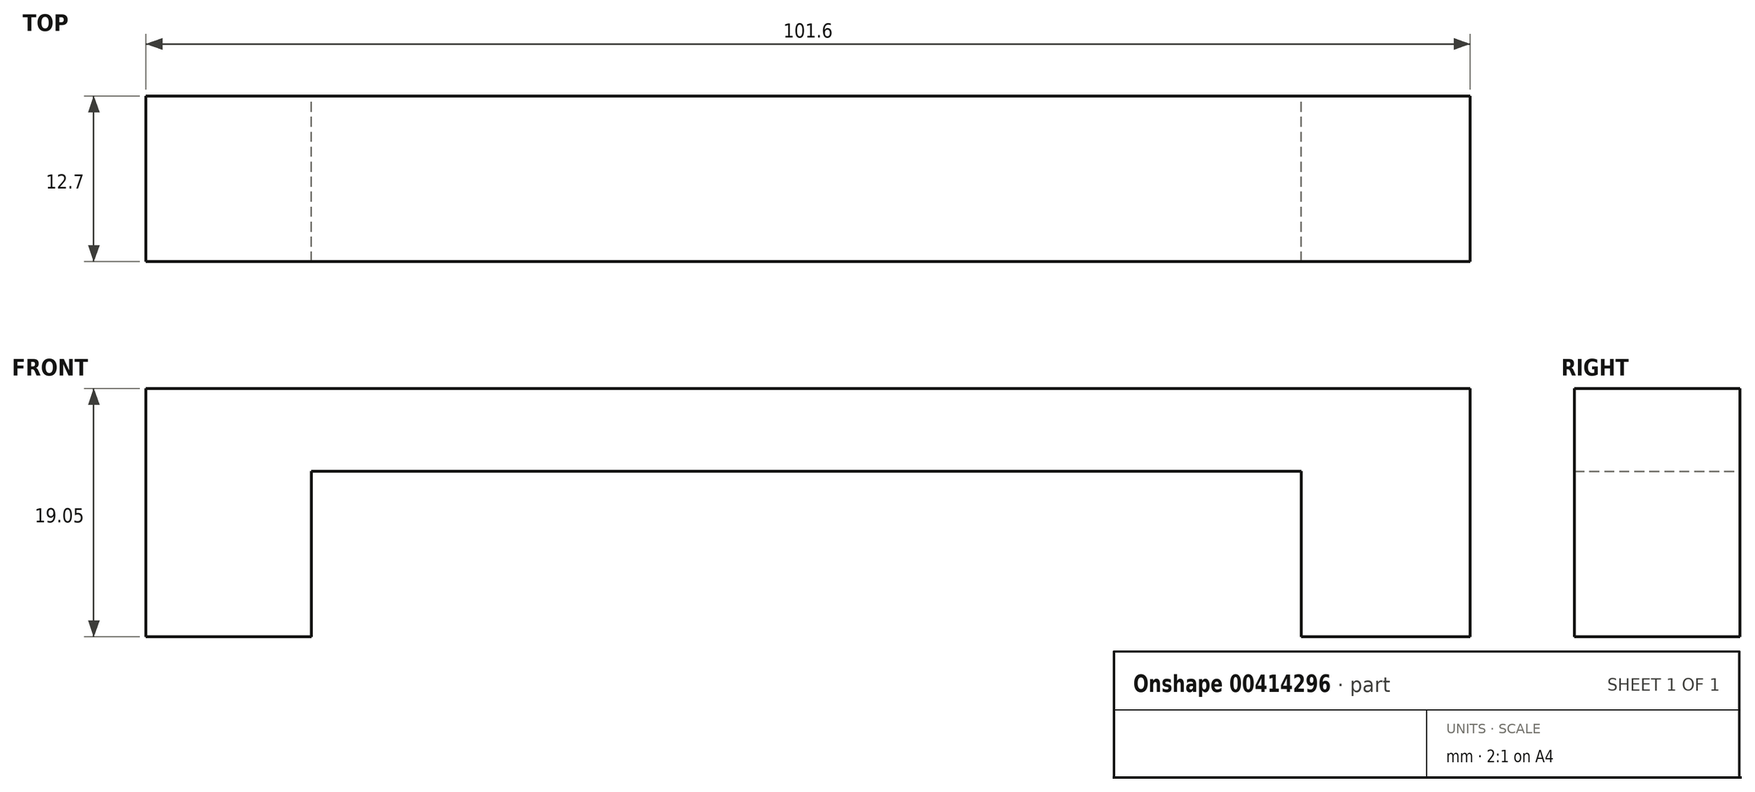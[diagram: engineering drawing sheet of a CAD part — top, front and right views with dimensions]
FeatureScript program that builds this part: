
annotation { "Feature Type Name" : "Feature", "Feature Type Description" : "" }
export const myFeature = defineFeature(function(context is Context, id is Id, definition is map)
    precondition{}
    {
        {
            var Q0;
            Q0=qCreatedBy(makeId("Front.planeOp"),FACE);
            var sketch = newSketch(context, id + "F0", { "sketchPlane" : qUnion([Q0])});
            skLineSegment(sketch, "E0", {"start": v(0, 0) * mm, "end": v(0, 19.05) * mm});
            skLineSegment(sketch, "E1", {"start": v(0, 19.05) * mm, "end": v(-101.6, 19.05) * mm});
            skLineSegment(sketch, "E2", {"start": v(-101.6, 19.05) * mm, "end": v(-101.6, 0) * mm});
            skLineSegment(sketch, "E3", {"start": v(-101.6, 0) * mm, "end": v(-88.9, 0) * mm});
            skLineSegment(sketch, "E4", {"start": v(-88.9, 0) * mm, "end": v(-88.9, 12.7) * mm});
            skLineSegment(sketch, "E5", {"start": v(-88.9, 12.7) * mm, "end": v(-12.98, 12.7) * mm});
            skLineSegment(sketch, "E6", {"start": v(-12.98, 12.7) * mm, "end": v(-12.98, 0) * mm});
            skLineSegment(sketch, "E7", {"start": v(-12.98, 0) * mm, "end": v(0, 0) * mm});
            skSolve(sketch);
        }
        {
            var Q0;
            Q0 = qSketchRegion(id + "F0", true);
            extrude(context, id + "F1", {"entities" : qUnion([Q0]), "depth" : 12.7 * mm});
        }
    });
